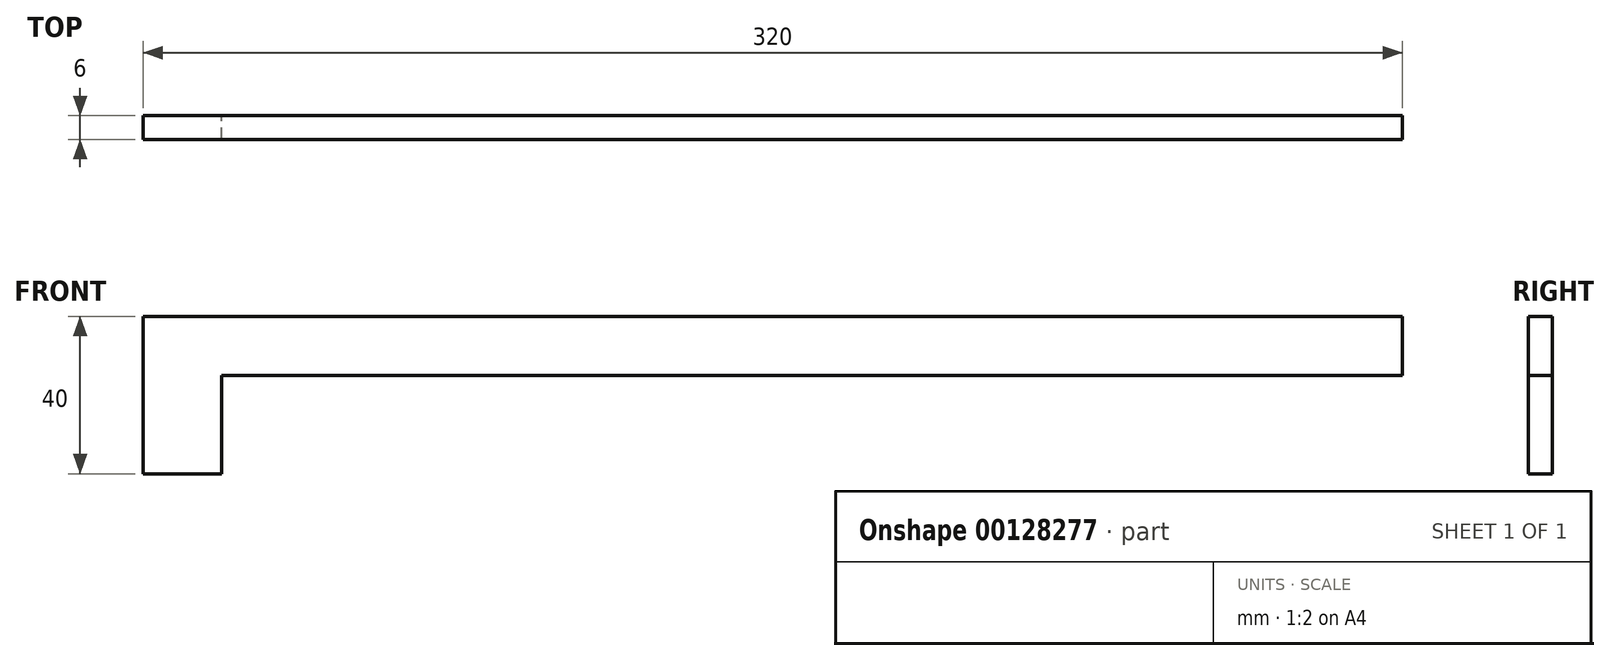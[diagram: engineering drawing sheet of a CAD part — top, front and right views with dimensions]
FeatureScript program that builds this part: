
annotation { "Feature Type Name" : "Feature", "Feature Type Description" : "" }
export const myFeature = defineFeature(function(context is Context, id is Id, definition is map)
    precondition{}
    {
        {
            var Q0;
            Q0=qCreatedBy(makeId("Front.planeOp"),FACE);
            var sketch = newSketch(context, id + "F0", { "sketchPlane" : qUnion([Q0])});
            skLineSegment(sketch, "E0", {"start": v(67.34, 52.88) * mm, "end": v(-209.74, 52.88) * mm});
            skLineSegment(sketch, "E1", {"start": v(-229.74, 52.88) * mm, "end": v(-229.74, 67.88) * mm});
            skLineSegment(sketch, "E2", {"start": v(-229.74, 67.88) * mm, "end": v(90.26, 67.88) * mm});
            skLineSegment(sketch, "E3", {"start": v(90.26, 67.88) * mm, "end": v(90.26, 52.88) * mm});
            skLineSegment(sketch, "E4", {"start": v(-229.74, 52.88) * mm, "end": v(-229.74, 27.88) * mm});
            skLineSegment(sketch, "E5", {"start": v(-229.74, 27.88) * mm, "end": v(-209.74, 27.88) * mm});
            skLineSegment(sketch, "E6", {"start": v(-209.74, 27.88) * mm, "end": v(-209.74, 52.88) * mm});
            skLineSegment(sketch, "E7", {"start": v(67.34, 52.88) * mm, "end": v(90.26, 52.88) * mm});
            skSolve(sketch);
        }
        {
            var Q0;
            Q0 = qSketchRegion(id + "F0", true);
            var Q1;
            Q1=makeQuery(id+"F0.imprint","IMPRINT",FACE,{"disambiguationData":[TD([[makeQuery(id+"F0.imprint","IMPRINT",EDGE,{"derivedFrom":sQuery(id+"F0.wireOp",EDGE,"E0")}),-1.0]])]});
            extrude(context, id + "F1", {"entities" : qUnion([Q0, Q1]), "depth" : 6 * mm});
        }
    });
